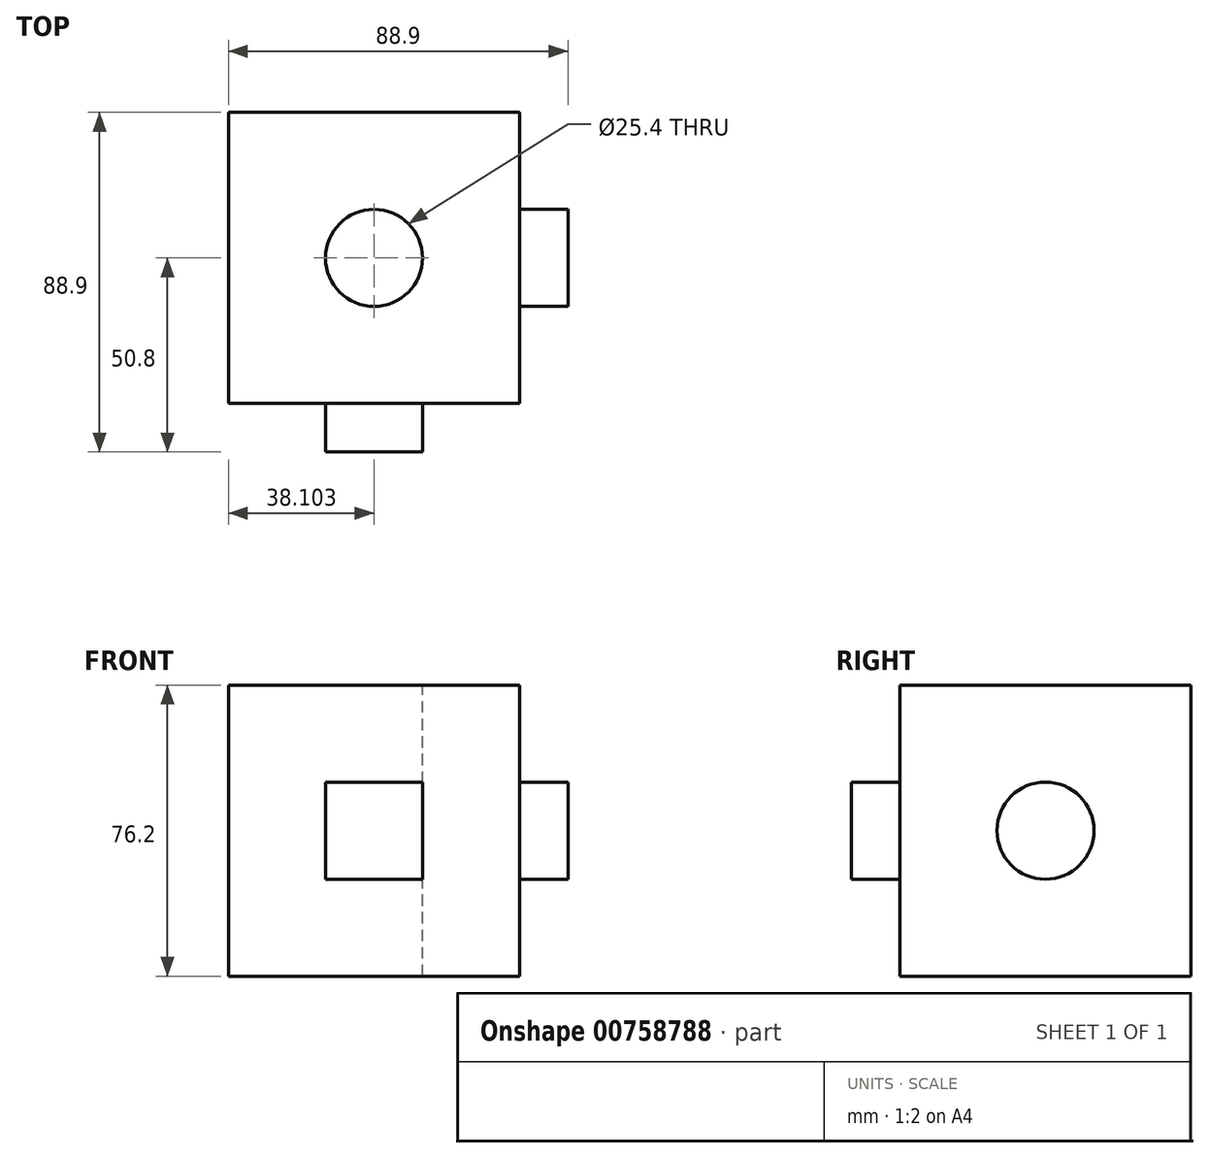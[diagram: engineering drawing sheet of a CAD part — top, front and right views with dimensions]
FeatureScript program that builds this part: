
annotation { "Feature Type Name" : "Feature", "Feature Type Description" : "" }
export const myFeature = defineFeature(function(context is Context, id is Id, definition is map)
    precondition{}
    {
        {
            var Q0;
            Q0=qCreatedBy(makeId("Front.planeOp"),FACE);
            var sketch = newSketch(context, id + "F0", { "sketchPlane" : qUnion([Q0])});
            skLineSegment(sketch, "E0.bottom", {"start": v(-52.99, 40.89) * mm, "end": v(23.21, 40.89) * mm});
            skLineSegment(sketch, "E0.top", {"start": v(-52.99, -35.31) * mm, "end": v(23.21, -35.31) * mm});
            skLineSegment(sketch, "E0.left", {"start": v(-52.99, 40.89) * mm, "end": v(-52.99, -35.31) * mm});
            skLineSegment(sketch, "E0.right", {"start": v(23.21, 40.89) * mm, "end": v(23.21, -35.31) * mm});
            skLineSegment(sketch, "E1.bottom", {"start": v(23.21, -35.31) * mm, "end": v(23.21, -35.31) * mm});
            skLineSegment(sketch, "E1.top", {"start": v(23.21, -20) * mm, "end": v(23.21, -20) * mm});
            skLineSegment(sketch, "E1.left", {"start": v(23.21, -35.31) * mm, "end": v(23.21, -20) * mm});
            skLineSegment(sketch, "E1.right", {"start": v(23.21, -35.31) * mm, "end": v(23.21, -20) * mm});
            skSolve(sketch);
        }
        {
            var Q0;
            Q0=makeQuery(id+"F0.imprint","IMPRINT",FACE,{"disambiguationData":[TD([[makeQuery(id+"F0.imprint","IMPRINT",EDGE,{"derivedFrom":sQuery(id+"F0.wireOp",EDGE,"E0.bottom")}),-1.0]])]});
            extrude(context, id + "F1", {"entities" : qUnion([Q0]), "depth" : 76.2 * mm, "offsetDistance" : 25.4 * mm});
        }
        {
            var Q0;
            Q0=makeQuery(id+"F1.opExtrude","CAP_FACE",FACE,{"disambiguationData":[OSD([sQuery(id+"F0.wireOp",EDGE,"E0.bottom"),sQuery(id+"F0.wireOp",EDGE,"E0.top"),sQuery(id+"F0.wireOp",EDGE,"E0.left"),sQuery(id+"F0.wireOp",EDGE,"E0.right"),sQuery(id+"F0.wireOp",EDGE,"E1.right")])],"isStart":false});
            var sketch = newSketch(context, id + "F2", { "sketchPlane" : qUnion([Q0])});
            skLineSegment(sketch, "E2.bottom", {"start": v(-27.59, 15.49) * mm, "end": v(-2.19, 15.49) * mm});
            skLineSegment(sketch, "E2.top", {"start": v(-27.59, -9.91) * mm, "end": v(-2.19, -9.91) * mm});
            skLineSegment(sketch, "E2.left", {"start": v(-27.59, 15.49) * mm, "end": v(-27.59, -9.91) * mm});
            skLineSegment(sketch, "E2.right", {"start": v(-2.19, 15.49) * mm, "end": v(-2.19, -9.91) * mm});
            skLineSegment(sketch, "E3.right", {"start": v(-2.19, 2.79) * mm, "end": v(-2.19, 5.2) * mm});
            skSolve(sketch);
        }
        {
            var Q0;
            {var subQ1=sQuery(id+"F2.wireOp",EDGE,"E2.bottom");Q0=makeQuery(id+"F2.imprint","IMPRINT",FACE,{"disambiguationData":[TD([[makeQuery(id+"F2.imprint","IMPRINT",EDGE,{"derivedFrom":subQ1}),-1.0]])]});}
            extrude(context, id + "F3", {"entities" : qUnion([Q0]), "operationType" : NewBodyOperationType.ADD, "depth" : 12.7 * mm, "offsetDistance" : 25.4 * mm});
        }
        {
            var Q0;
            Q0=makeQuery(id+"F1.opExtrude","SWEPT_FACE",FACE,{"disambiguationData":[OSD([sQuery(id+"F0.wireOp",EDGE,"E0.right"),sQuery(id+"F0.wireOp",EDGE,"E1.right")])]});
            var sketch = newSketch(context, id + "F4", { "sketchPlane" : qUnion([Q0])});
            skCircle(sketch, "E4", {"center": v(-38.1, 2.79) * mm, "radius": 12.7 * mm});
            skSolve(sketch);
        }
        {
            var Q0;
            Q0=makeQuery(id+"F4.imprint","IMPRINT",FACE,{"disambiguationData":[TD([[makeQuery(id+"F4.imprint","IMPRINT",EDGE,{"derivedFrom":sQuery(id+"F4.wireOp",EDGE,"E4")}),1.0]])]});
            extrude(context, id + "F5", {"entities" : qUnion([Q0]), "operationType" : NewBodyOperationType.ADD, "depth" : 12.7 * mm, "offsetDistance" : 25.4 * mm});
        }
        {
            var Q0;
            Q0=makeQuery(id+"F1.opExtrude","SWEPT_FACE",FACE,{"disambiguationData":[OSD([sQuery(id+"F0.wireOp",EDGE,"E0.bottom")])]});
            var sketch = newSketch(context, id + "F6", { "sketchPlane" : qUnion([Q0])});
            skPoint(sketch, "E5", {"position": v(-14.89, -38.1) * mm});
            skSolve(sketch);
        }
        {
            var Q0;
            Q0=sQuery(id+"F6.wireOp",VERTEX,"E5");
            var Q1;
            Q1=makeQuery(id+"F1.opExtrude","SWEPT_BODY",BODY,{"disambiguationData":[OSD([sQuery(id+"F0.wireOp",EDGE,"E0.bottom"),sQuery(id+"F0.wireOp",EDGE,"E0.top"),sQuery(id+"F0.wireOp",EDGE,"E0.left"),sQuery(id+"F0.wireOp",EDGE,"E0.right"),sQuery(id+"F0.wireOp",EDGE,"E1.right")])]});
            hole(context, id + "F7", {"style" : HoleStyle.SIMPLE, "endStyle" : HoleEndStyle.THROUGH, "holeDiameter" : 25.4 * mm, "majorDiameter" : 6.35 * mm, "isTappedThrough" : true, "tappedDepth" : 12.7 * mm, "tapClearance" : 3, "locations" : qUnion([Q0]), "scope" : qUnion([Q1])});
        }
    });
